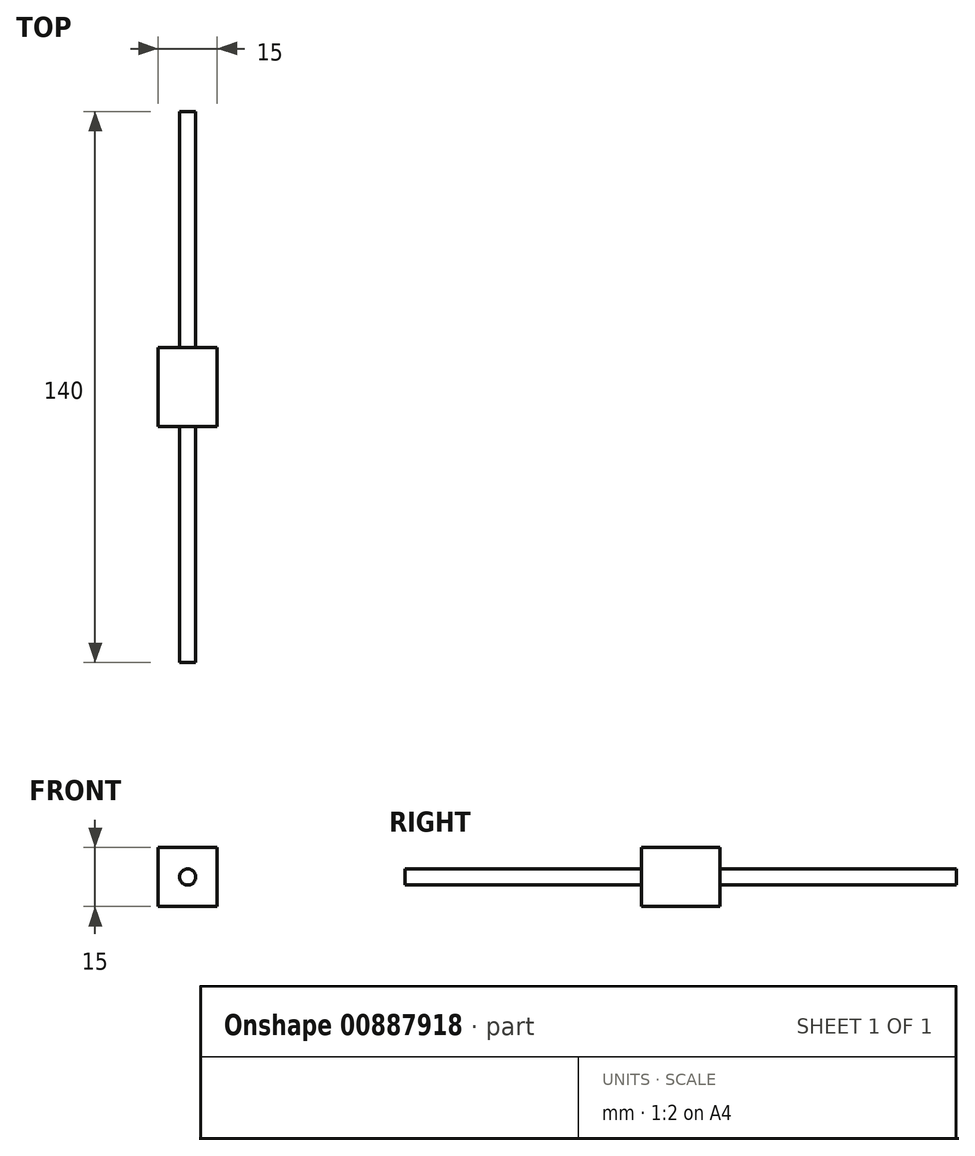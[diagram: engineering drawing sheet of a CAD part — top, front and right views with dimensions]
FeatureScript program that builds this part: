
annotation { "Feature Type Name" : "Feature", "Feature Type Description" : "" }
export const myFeature = defineFeature(function(context is Context, id is Id, definition is map)
    precondition{}
    {
        {
            var Q0;
            Q0=qCreatedBy(makeId("Front.planeOp"),FACE);
            var sketch = newSketch(context, id + "F0", { "sketchPlane" : qUnion([Q0])});
            skCircle(sketch, "E0", {"center": v(0, 0) * mm, "radius": 2.05 * mm});
            skSolve(sketch);
        }
        {
            var Q0;
            Q0 = qSketchRegion(id + "F0", true);
            extrude(context, id + "F1", {"entities" : qUnion([Q0]), "endBound" : BoundingType.SYMMETRIC, "depth" : 140 * mm, "offsetDistance" : 25 * mm});
        }
        {
            var Q0;
            Q0=qCreatedBy(makeId("Right.planeOp"),FACE);
            var sketch = newSketch(context, id + "F2", { "sketchPlane" : qUnion([Q0])});
            skLineSegment(sketch, "E1.bottom", {"start": v(10, 7.5) * mm, "end": v(-10, 7.5) * mm});
            skLineSegment(sketch, "E1.top", {"start": v(10, -7.5) * mm, "end": v(-10, -7.5) * mm});
            skLineSegment(sketch, "E1.left", {"start": v(10, 7.5) * mm, "end": v(10, -7.5) * mm});
            skLineSegment(sketch, "E1.right", {"start": v(-10, 7.5) * mm, "end": v(-10, -7.5) * mm});
            skPoint(sketch, "E1.middle", {"position": v(0, 0) * mm});
            skSolve(sketch);
        }
        {
            var Q0;
            Q0 = qSketchRegion(id + "F2", true);
            extrude(context, id + "F3", {"entities" : qUnion([Q0]), "operationType" : NewBodyOperationType.ADD, "endBound" : BoundingType.SYMMETRIC, "depth" : 15 * mm, "offsetDistance" : 25 * mm});
        }
    });
